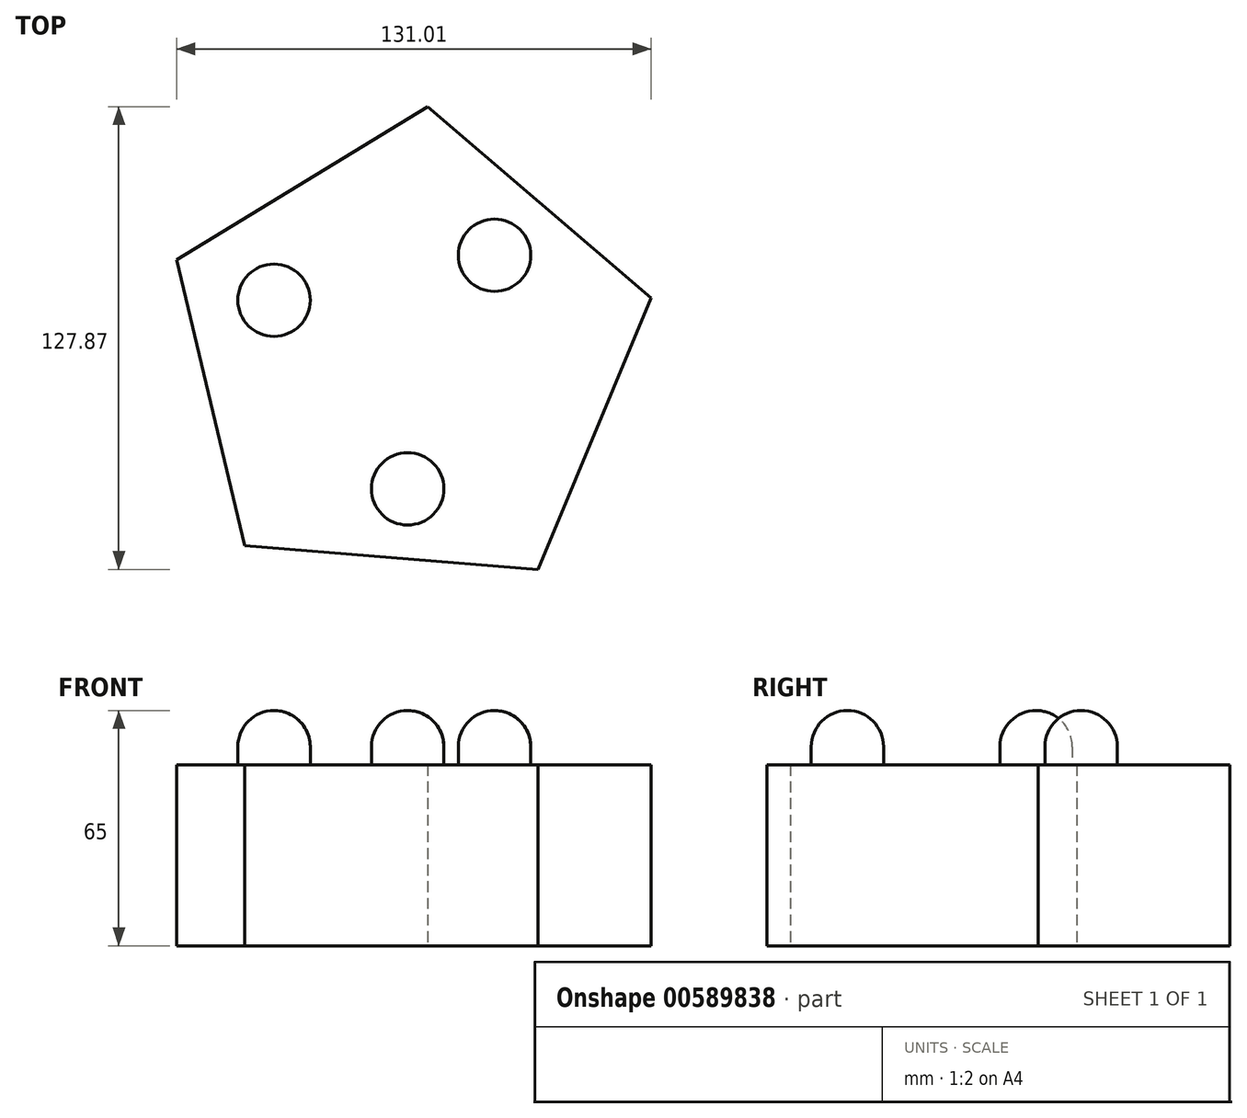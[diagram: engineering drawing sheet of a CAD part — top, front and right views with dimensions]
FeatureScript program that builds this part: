
annotation { "Feature Type Name" : "Feature", "Feature Type Description" : "" }
export const myFeature = defineFeature(function(context is Context, id is Id, definition is map)
    precondition{}
    {
        {
            var Q0;
            Q0=qCreatedBy(makeId("Top.planeOp"),FACE);
            var sketch = newSketch(context, id + "F0", { "sketchPlane" : qUnion([Q0])});
            skCircle(sketch, "E0.cCircle", {"center": v(0, 0) * mm, "radius": 55.9 * mm, "construction": true});
            skLineSegment(sketch, "E0.0", {"start": v(67.23, 15.97) * mm, "end": v(35.96, -59) * mm});
            skLineSegment(sketch, "E0.1", {"start": v(35.96, -59) * mm, "end": v(-45, -52.44) * mm});
            skLineSegment(sketch, "E0.2", {"start": v(-45, -52.44) * mm, "end": v(-63.78, 26.6) * mm});
            skLineSegment(sketch, "E0.3", {"start": v(-63.78, 26.6) * mm, "end": v(5.58, 68.87) * mm});
            skLineSegment(sketch, "E0.4", {"start": v(5.58, 68.87) * mm, "end": v(67.23, 15.97) * mm});
            skPoint(sketch, "E0.0.midPoint", {"position": v(51.6, -21.51) * mm});
            skCircle(sketch, "E1", {"center": v(24, 27.81) * mm, "radius": 10 * mm});
            skCircle(sketch, "E2", {"center": v(0, -36.73) * mm, "radius": 10 * mm});
            skLineSegment(sketch, "E3", {"start": v(-63.78, 26.6) * mm, "end": v(0, 0) * mm});
            skCircle(sketch, "E4", {"center": v(-36.92, 15.4) * mm, "radius": 10 * mm});
            skSolve(sketch);
        }
        {
            var Q0;
            Q0=makeQuery(id+"F0.imprint","IMPRINT",FACE,{"disambiguationData":[TD([[makeQuery(id+"F0.imprint","IMPRINT",EDGE,{"derivedFrom":sQuery(id+"F0.wireOp",EDGE,"E0.0")}),-1.0]])]});
            extrude(context, id + "F1", {"entities" : qUnion([Q0]), "depth" : 50 * mm, "offsetDistance" : 25 * mm});
        }
        {
            var Q0;
            {var subQ0=sQuery(id+"F0.wireOp",EDGE,"E4");var subQ1=sQuery(id+"F0.wireOp",EDGE,"E3");var subQ2=makeQuery(id+"F0.imprint","INTERSECT",VERTEX,{"disambiguationData":[OD(0.0)],"derivedFrom":[subQ1,subQ0]});Q0=makeQuery(id+"F0.imprint","IMPRINT",FACE,{"disambiguationData":[TD([[makeQuery(id+"F0.imprint","IMPRINT",EDGE,{"disambiguationData":[TD([[subQ2,-1.0]])],"derivedFrom":subQ1}),-1.0]])]});}
            var Q1;
            {var subQ0=sQuery(id+"F0.wireOp",EDGE,"E4");var subQ1=sQuery(id+"F0.wireOp",EDGE,"E3");var subQ2=makeQuery(id+"F0.imprint","INTERSECT",VERTEX,{"disambiguationData":[OD(0.0)],"derivedFrom":[subQ1,subQ0]});Q1=makeQuery(id+"F0.imprint","IMPRINT",FACE,{"disambiguationData":[TD([[makeQuery(id+"F0.imprint","IMPRINT",EDGE,{"disambiguationData":[TD([[subQ2,-1.0]])],"derivedFrom":subQ1}),1.0]])]});}
            var Q2;
            Q2=makeQuery(id+"F0.imprint","IMPRINT",FACE,{"disambiguationData":[TD([[makeQuery(id+"F0.imprint","IMPRINT",EDGE,{"derivedFrom":sQuery(id+"F0.wireOp",EDGE,"E1")}),1.0]])]});
            var Q3;
            Q3=makeQuery(id+"F0.imprint","IMPRINT",FACE,{"disambiguationData":[TD([[makeQuery(id+"F0.imprint","IMPRINT",EDGE,{"derivedFrom":sQuery(id+"F0.wireOp",EDGE,"E2")}),1.0]])]});
            extrude(context, id + "F2", {"entities" : qUnion([Q0, Q1, Q2, Q3]), "operationType" : NewBodyOperationType.ADD, "depth" : 65 * mm, "offsetDistance" : 25 * mm});
        }
        {
            var Q0;
            Q0=makeQuery(id+"F2.opExtrude","CAP_EDGE",EDGE,{"disambiguationData":[OSD([sQuery(id+"F0.wireOp",EDGE,"E4")])],"isStart":false});
            var Q1;
            Q1=makeQuery(id+"F2.opExtrude","CAP_EDGE",EDGE,{"disambiguationData":[OSD([sQuery(id+"F0.wireOp",EDGE,"E2")])],"isStart":false});
            var Q2;
            Q2=makeQuery(id+"F2.opExtrude","CAP_EDGE",EDGE,{"disambiguationData":[OSD([sQuery(id+"F0.wireOp",EDGE,"E1")])],"isStart":false});
            fillet(context, id + "F3", {"entities" : qUnion([Q0, Q1, Q2]), "radius" : 10 * mm, "tangentPropagation" : true, "allowEdgeOverflow" : false});
        }
    });
